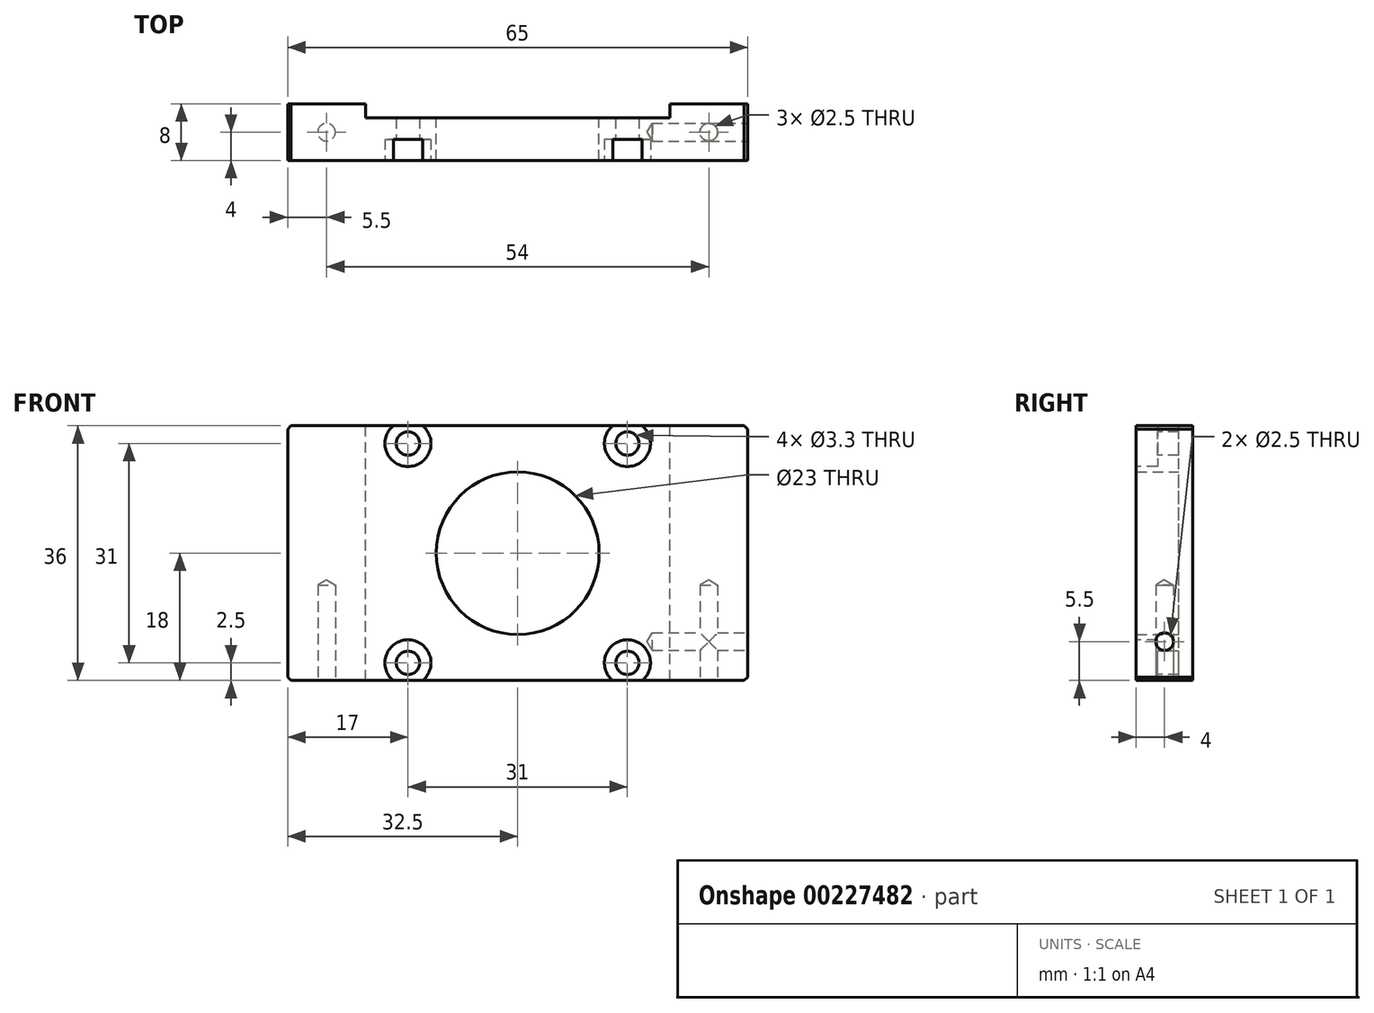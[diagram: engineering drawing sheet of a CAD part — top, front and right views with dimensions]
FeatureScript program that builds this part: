
annotation { "Feature Type Name" : "Feature", "Feature Type Description" : "" }
export const myFeature = defineFeature(function(context is Context, id is Id, definition is map)
    precondition{}
    {
        {
            var Q0;
            Q0=qCreatedBy(makeId("Front.planeOp"),FACE);
            var sketch = newSketch(context, id + "F0", { "sketchPlane" : qUnion([Q0])});
            skLineSegment(sketch, "E0.bottom", {"start": v(32.5, -18) * mm, "end": v(-32.5, -18) * mm});
            skLineSegment(sketch, "E0.top", {"start": v(32.5, 18) * mm, "end": v(-32.5, 18) * mm});
            skLineSegment(sketch, "E0.left", {"start": v(32.5, -18) * mm, "end": v(32.5, 18) * mm});
            skLineSegment(sketch, "E0.right", {"start": v(-32.5, -18) * mm, "end": v(-32.5, 18) * mm});
            skPoint(sketch, "E0.middle", {"position": v(0, 0) * mm});
            skCircle(sketch, "E1", {"center": v(0, 0) * mm, "radius": 11.5 * mm});
            skSolve(sketch);
        }
        {
            var Q0;
            Q0=makeQuery(id+"F0.imprint","IMPRINT",FACE,{"disambiguationData":[TD([[makeQuery(id+"F0.imprint","IMPRINT",EDGE,{"derivedFrom":sQuery(id+"F0.wireOp",EDGE,"E0.bottom")}),-1.0]])]});
            extrude(context, id + "F1", {"entities" : qUnion([Q0]), "depth" : 8 * mm});
        }
        {
            var Q0;
            Q0=makeQuery(id+"F1.opExtrude","CAP_FACE",FACE,{"disambiguationData":[OSD([sQuery(id+"F0.wireOp",EDGE,"E0.bottom"),sQuery(id+"F0.wireOp",EDGE,"E0.top"),sQuery(id+"F0.wireOp",EDGE,"E0.left"),sQuery(id+"F0.wireOp",EDGE,"E0.right")])],"isStart":false});
            var sketch = newSketch(context, id + "F2", { "sketchPlane" : qUnion([Q0])});
            skPoint(sketch, "E2", {"position": v(15.5, 15.5) * mm});
            skPoint(sketch, "E3.MirrorP", {"position": v(-15.5, 15.5) * mm});
            skPoint(sketch, "E4.MirrorP", {"position": v(15.5, -15.5) * mm});
            skPoint(sketch, "E5.MirrorP", {"position": v(-15.5, -15.5) * mm});
            skSolve(sketch);
        }
        {
            var Q0;
            Q0=sQuery(id+"F2.wireOp",VERTEX,"E2");
            var Q1;
            Q1=sQuery(id+"F2.wireOp",VERTEX,"E4.MirrorP");
            var Q2;
            Q2=sQuery(id+"F2.wireOp",VERTEX,"E5.MirrorP");
            var Q3;
            Q3=sQuery(id+"F2.wireOp",VERTEX,"E3.MirrorP");
            var Q4;
            Q4=makeQuery(id+"F1.opExtrude","SWEPT_BODY",BODY,{"disambiguationData":[OSD([sQuery(id+"F0.wireOp",EDGE,"E0.bottom"),sQuery(id+"F0.wireOp",EDGE,"E0.top"),sQuery(id+"F0.wireOp",EDGE,"E0.left"),sQuery(id+"F0.wireOp",EDGE,"E0.right")])]});
            hole(context, id + "F3", {"style" : HoleStyle.C_BORE, "endStyle" : HoleEndStyle.THROUGH, "standardTappedOrClearance" : lookupTablePath({ "standard" : "ISO", "fit" : "Normal", "size" : "M3", "type" : "Clearance" }), "standardBlindInLast" : lookupTablePath({ "fit" : "Standard", "standard" : "ISO", "size" : "M3", "type" : "Clearance" }), "holeDiameter" : 3.3 * mm, "cBoreDiameter" : 6.5 * mm, "cBoreDepth" : 3 * mm, "locations" : qUnion([Q0, Q1, Q2, Q3]), "scope" : qUnion([Q4]), "isTappedThrough" : true});
        }
        {
            var Q0;
            Q0=makeQuery(id+"F1.opExtrude","SWEPT_EDGE",EDGE,{"disambiguationData":[OSD([sQuery(id+"F0.wireOp",EDGE,"E0.top"),sQuery(id+"F0.wireOp",EDGE,"E0.right")])]});
            var Q1;
            Q1=makeQuery(id+"F1.opExtrude","SWEPT_EDGE",EDGE,{"disambiguationData":[OSD([sQuery(id+"F0.wireOp",EDGE,"E0.top"),sQuery(id+"F0.wireOp",EDGE,"E0.left")])]});
            var Q2;
            Q2=makeQuery(id+"F1.opExtrude","SWEPT_EDGE",EDGE,{"disambiguationData":[OSD([sQuery(id+"F0.wireOp",EDGE,"E0.bottom"),sQuery(id+"F0.wireOp",EDGE,"E0.left")])]});
            var Q3;
            Q3=makeQuery(id+"F1.opExtrude","SWEPT_EDGE",EDGE,{"disambiguationData":[OSD([sQuery(id+"F0.wireOp",EDGE,"E0.bottom"),sQuery(id+"F0.wireOp",EDGE,"E0.right")])]});
            chamfer(context, id + "F4", {"entities" : qUnion([Q0, Q1, Q2, Q3]), "width" : 0.5 * mm, "tangentPropagation" : true});
        }
        {
            var Q0;
            Q0=makeQuery(id+"F1.opExtrude","SWEPT_FACE",FACE,{"disambiguationData":[OSD([sQuery(id+"F0.wireOp",EDGE,"E0.bottom")])]});
            var sketch = newSketch(context, id + "F5", { "sketchPlane" : qUnion([Q0])});
            skPoint(sketch, "E6", {"position": v(27, 4) * mm});
            skPoint(sketch, "E7.MirrorP", {"position": v(-27, 4) * mm});
            skSolve(sketch);
        }
        {
            var Q0;
            Q0=sQuery(id+"F5.wireOp",VERTEX,"E6");
            var Q1;
            Q1=sQuery(id+"F5.wireOp",VERTEX,"E7.MirrorP");
            var Q2;
            Q2=makeQuery(id+"F1.opExtrude","SWEPT_BODY",BODY,{"disambiguationData":[OSD([sQuery(id+"F0.wireOp",EDGE,"E0.bottom"),sQuery(id+"F0.wireOp",EDGE,"E0.top"),sQuery(id+"F0.wireOp",EDGE,"E0.left"),sQuery(id+"F0.wireOp",EDGE,"E0.right"),sQuery(id+"F0.wireOp",EDGE,"E1")])]});
            hole(context, id + "F6", {"style" : HoleStyle.SIMPLE, "endStyle" : HoleEndStyle.BLIND, "standardTappedOrClearance" : lookupTablePath({ "standard" : "ISO", "engagement" : "75%", "pitch" : "0.5 mm", "size" : "M3", "type" : "Tapped" }), "standardBlindInLast" : lookupTablePath({ "standard" : "ISO", "engagement" : "75%", "pitch" : "0.5 mm", "size" : "M3", "type" : "Tapped" }), "holeDiameter" : 2.5 * mm, "holeDepth" : 13.5 * mm, "locations" : qUnion([Q0, Q1]), "scope" : qUnion([Q2]), "showTappedDepth" : true, "tappedDepth" : 12 * mm, "tapClearance" : 3, "majorDiameter" : 3 * mm});
        }
        {
            var Q0;
            Q0=makeQuery(id+"F1.opExtrude","CAP_FACE",FACE,{"disambiguationData":[OSD([sQuery(id+"F0.wireOp",EDGE,"E0.bottom"),sQuery(id+"F0.wireOp",EDGE,"E0.top"),sQuery(id+"F0.wireOp",EDGE,"E0.left"),sQuery(id+"F0.wireOp",EDGE,"E0.right"),sQuery(id+"F0.wireOp",EDGE,"E1")])],"isStart":true});
            var sketch = newSketch(context, id + "F7", { "sketchPlane" : qUnion([Q0])});
            skLineSegment(sketch, "E8.bottom", {"start": v(21.5, -18) * mm, "end": v(-21.5, -18) * mm});
            skLineSegment(sketch, "E8.top", {"start": v(21.5, 18) * mm, "end": v(-21.5, 18) * mm});
            skLineSegment(sketch, "E8.left", {"start": v(21.5, -18) * mm, "end": v(21.5, 18) * mm});
            skLineSegment(sketch, "E8.right", {"start": v(-21.5, -18) * mm, "end": v(-21.5, 18) * mm});
            skPoint(sketch, "E8.middle", {"position": v(0, 0) * mm});
            skSolve(sketch);
        }
        {
            var Q0;
            Q0=makeQuery(id+"F7.imprint","IMPRINT",FACE,{"disambiguationData":[TD([[makeQuery(id+"F7.imprint","IMPRINT",EDGE,{"derivedFrom":sQuery(id+"F7.wireOp",EDGE,"E8.bottom")}),1.0]])]});
            extrude(context, id + "F8", {"entities" : qUnion([Q0]), "operationType" : NewBodyOperationType.REMOVE, "oppositeDirection" : true, "depth" : 2 * mm});
        }
        {
            var Q0;
            Q0=makeQuery(id+"F1.opExtrude","SWEPT_FACE",FACE,{"disambiguationData":[OSD([sQuery(id+"F0.wireOp",EDGE,"E0.left")])]});
            var sketch = newSketch(context, id + "F9", { "sketchPlane" : qUnion([Q0])});
            skPoint(sketch, "E9", {"position": v(-4, -12.5) * mm});
            skPoint(sketch, "E9.positionSnap0", {"position": v(-4, -17.5) * mm});
            skSolve(sketch);
        }
        {
            var Q0;
            Q0=sQuery(id+"F9.wireOp",VERTEX,"E9");
            var Q1;
            Q1=makeQuery(id+"F1.opExtrude","SWEPT_BODY",BODY,{"disambiguationData":[OSD([sQuery(id+"F0.wireOp",EDGE,"E0.bottom"),sQuery(id+"F0.wireOp",EDGE,"E0.top"),sQuery(id+"F0.wireOp",EDGE,"E0.left"),sQuery(id+"F0.wireOp",EDGE,"E0.right"),sQuery(id+"F0.wireOp",EDGE,"E1")])]});
            hole(context, id + "F10", {"style" : HoleStyle.SIMPLE, "endStyle" : HoleEndStyle.BLIND, "standardTappedOrClearance" : lookupTablePath({ "standard" : "ISO", "engagement" : "75%", "pitch" : "0.5 mm", "size" : "M3", "type" : "Tapped" }), "standardBlindInLast" : lookupTablePath({ "standard" : "ISO", "engagement" : "75%", "pitch" : "0.5 mm", "size" : "M3", "type" : "Tapped" }), "holeDiameter" : 2.5 * mm, "showTappedDepth" : true, "holeDepth" : 13.5 * mm, "tappedDepth" : 12 * mm, "tapClearance" : 3, "locations" : qUnion([Q0]), "scope" : qUnion([Q1]), "majorDiameter" : 3 * mm});
        }
    });
